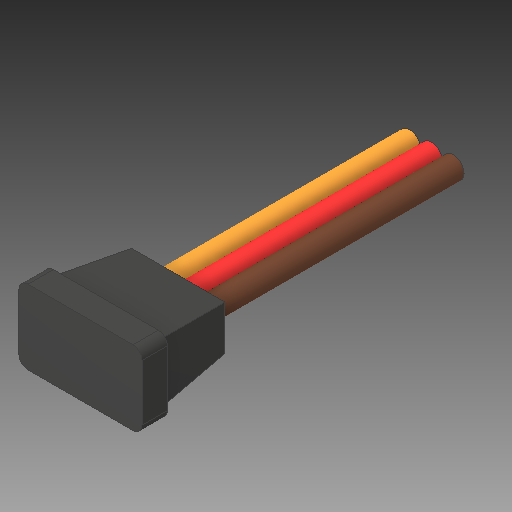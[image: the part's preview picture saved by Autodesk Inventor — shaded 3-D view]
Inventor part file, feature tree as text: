
AUTODESK INVENTOR PART (.ipt)
format: ipt  version: 2017 (Build 210142000, 142)  size: 116,224 bytes
history: native  units: in
note: dims shown in document units (in); Inventor stores cm internally (conversion verified against a paired STEP export)
features: other x3, fillet x1
ambient origin geometry x8: Origin, YZ Plane, XZ Plane, XY Plane, X Axis, Y Axis, Z Axis, Center Point
bodies: Solid1 (feature_tree), Solid2 (feature_tree), Solid3 (feature_tree), Solid4 (feature_tree)
feature tree (4):
  fillet  "Fillet1"  [1 undecoded]
  other  "POSITIVE"
  other  "SIGNAL"
  other  "NEGATIVE"
note: 1 required parameter value undecoded (feature->parameter linkage not recoverable at this tier; creation-order binding heuristic only, values carry confidence <= 0.55)
